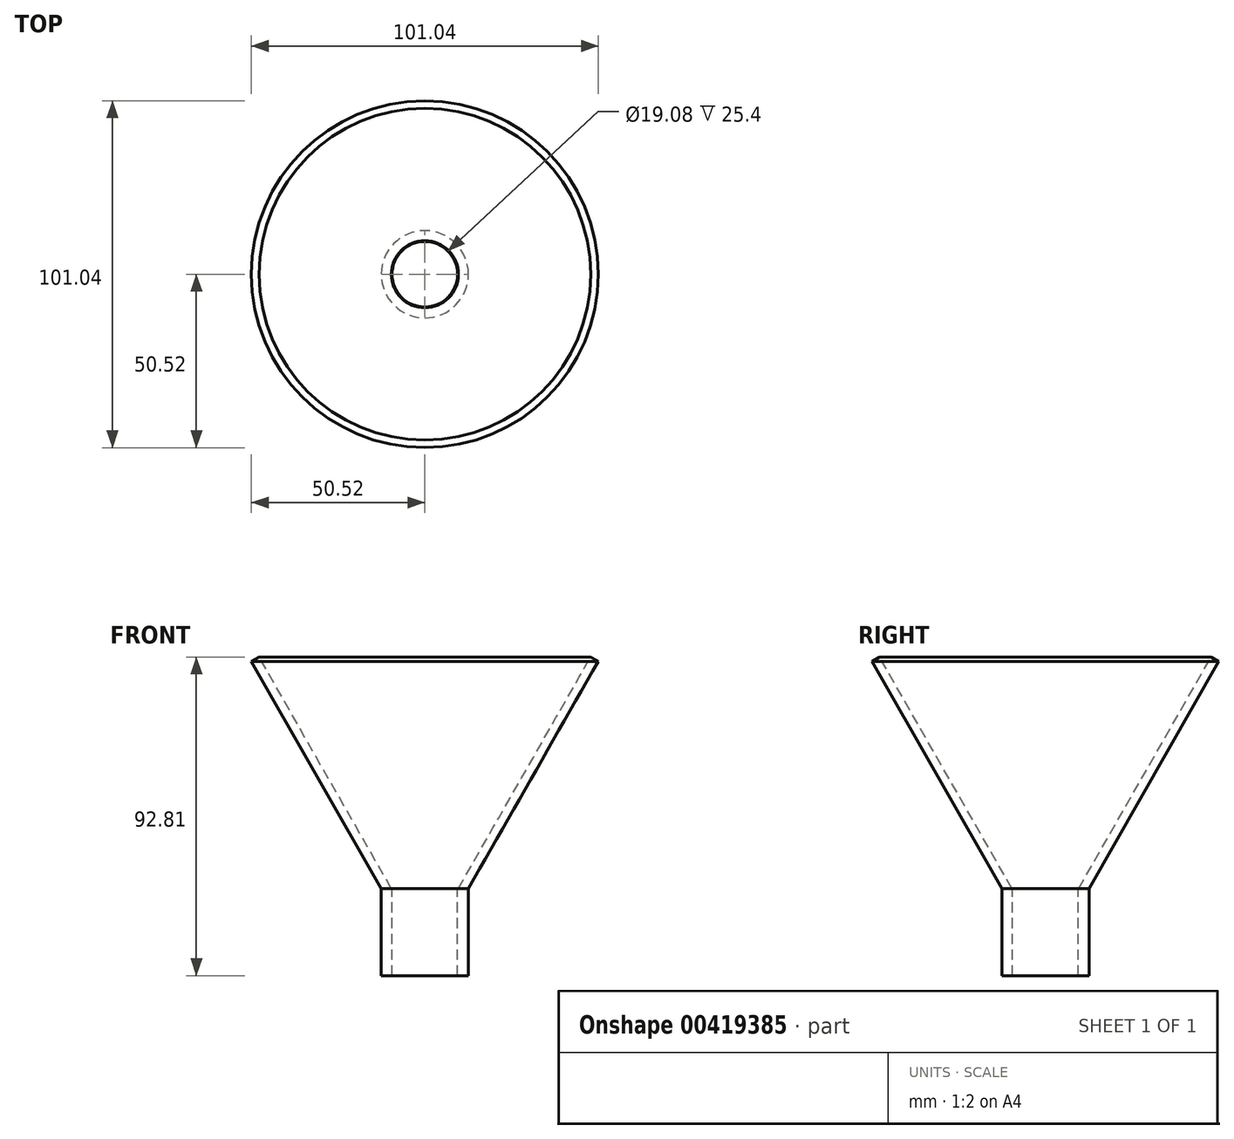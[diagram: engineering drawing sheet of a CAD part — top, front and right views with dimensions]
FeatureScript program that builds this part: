
annotation { "Feature Type Name" : "Feature", "Feature Type Description" : "" }
export const myFeature = defineFeature(function(context is Context, id is Id, definition is map)
    precondition{}
    {
        {
            var Q0;
            Q0=qCreatedBy(makeId("Front.planeOp"),FACE);
            var sketch = newSketch(context, id + "F0", { "sketchPlane" : qUnion([Q0])});
            skLineSegment(sketch, "E0.bottom", {"start": v(0, 0) * mm, "end": v(-12.7, 0) * mm});
            skLineSegment(sketch, "E0.top", {"start": v(0, -25.4) * mm, "end": v(-12.7, -25.4) * mm});
            skLineSegment(sketch, "E0.left", {"start": v(0, 0) * mm, "end": v(0, -25.4) * mm});
            skLineSegment(sketch, "E0.right", {"start": v(-12.7, 0) * mm, "end": v(-12.7, -25.4) * mm});
            skLineSegment(sketch, "E1", {"start": v(-12.7, 0) * mm, "end": v(-50.52, 66.15) * mm});
            skLineSegment(sketch, "E2", {"start": v(-50.52, 66.15) * mm, "end": v(-48.31, 67.41) * mm});
            skLineSegment(sketch, "E3", {"start": v(-48.31, 67.41) * mm, "end": v(-9.77, 0) * mm});
            skSolve(sketch);
        }
        {
            var Q0;
            Q0 = qSketchRegion(id + "F0", true);
            var Q1;
            Q1=sQuery(id+"F0.wireOp",EDGE,"E0.left");
            revolve(context, id + "F1", {"entities" : qUnion([Q0]), "axis" : qUnion([Q1]), "revolveType" : RevolveType.FULL});
        }
        {
            var Q0;
            Q0=makeQuery(id+"F1.opRevolve","SWEPT_FACE",FACE,{"disambiguationData":[OSD([sQuery(id+"F0.wireOp",EDGE,"E0.bottom")])]});
            var sketch = newSketch(context, id + "F2", { "sketchPlane" : qUnion([Q0])});
            skCircle(sketch, "E4", {"center": v(0, 0) * mm, "radius": 9.54 * mm});
            skSolve(sketch);
        }
        {
            var Q0;
            Q0 = qSketchRegion(id + "F2", true);
            extrude(context, id + "F3", {"entities" : qUnion([Q0]), "operationType" : NewBodyOperationType.REMOVE, "oppositeDirection" : true, "depth" : 25.4 * mm});
        }
    });
